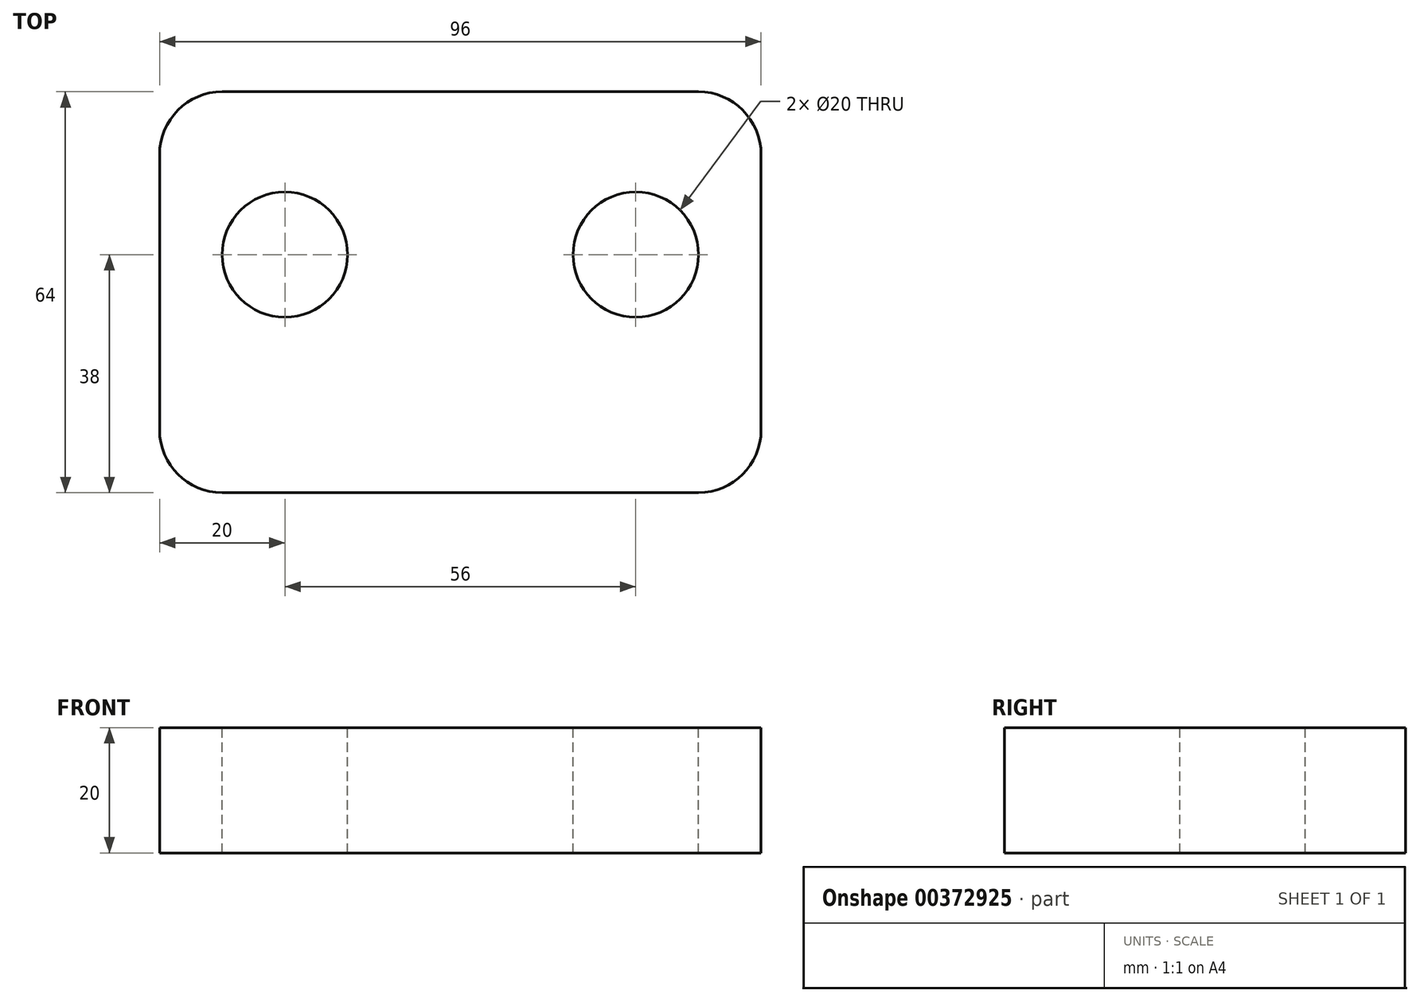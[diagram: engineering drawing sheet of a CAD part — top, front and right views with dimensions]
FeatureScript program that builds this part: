
annotation { "Feature Type Name" : "Feature", "Feature Type Description" : "" }
export const myFeature = defineFeature(function(context is Context, id is Id, definition is map)
    precondition{}
    {
        {
            var Q0;
            Q0=qCreatedBy(makeId("Top.planeOp"),FACE);
            var sketch = newSketch(context, id + "F0", { "sketchPlane" : qUnion([Q0])});
            skLineSegment(sketch, "E0.bottom", {"start": v(48, 32) * mm, "end": v(-48, 32) * mm});
            skLineSegment(sketch, "E0.top", {"start": v(48, -32) * mm, "end": v(-48, -32) * mm});
            skLineSegment(sketch, "E0.left", {"start": v(48, 32) * mm, "end": v(48, -32) * mm});
            skLineSegment(sketch, "E0.right", {"start": v(-48, 32) * mm, "end": v(-48, -32) * mm});
            skPoint(sketch, "E0.middle", {"position": v(0, 0) * mm});
            skSolve(sketch);
        }
        {
            var Q0;
            Q0 = qSketchRegion(id + "F0", true);
            extrude(context, id + "F1", {"entities" : qUnion([Q0]), "depth" : 20 * mm});
        }
        {
            var Q0;
            Q0=makeQuery(id+"F1.opExtrude","SWEPT_EDGE",EDGE,{"disambiguationData":[OSD([sQuery(id+"F0.wireOp",EDGE,"E0.top"),sQuery(id+"F0.wireOp",EDGE,"E0.left")])]});
            var Q1;
            Q1=makeQuery(id+"F1.opExtrude","SWEPT_EDGE",EDGE,{"disambiguationData":[OSD([sQuery(id+"F0.wireOp",EDGE,"E0.bottom"),sQuery(id+"F0.wireOp",EDGE,"E0.left")])]});
            var Q2;
            Q2=makeQuery(id+"F1.opExtrude","SWEPT_EDGE",EDGE,{"disambiguationData":[OSD([sQuery(id+"F0.wireOp",EDGE,"E0.bottom"),sQuery(id+"F0.wireOp",EDGE,"E0.right")])]});
            var Q3;
            Q3=makeQuery(id+"F1.opExtrude","SWEPT_EDGE",EDGE,{"disambiguationData":[OSD([sQuery(id+"F0.wireOp",EDGE,"E0.top"),sQuery(id+"F0.wireOp",EDGE,"E0.right")])]});
            fillet(context, id + "F2", {"entities" : qUnion([Q0, Q1, Q2, Q3]), "radius" : 10 * mm, "tangentPropagation" : true, "allowEdgeOverflow" : false});
        }
        {
            var Q0;
            Q0=makeQuery(id+"F1.opExtrude","CAP_FACE",FACE,{"disambiguationData":[OSD([sQuery(id+"F0.wireOp",EDGE,"E0.bottom"),sQuery(id+"F0.wireOp",EDGE,"E0.top"),sQuery(id+"F0.wireOp",EDGE,"E0.left"),sQuery(id+"F0.wireOp",EDGE,"E0.right")])],"isStart":false});
            var sketch = newSketch(context, id + "F3", { "sketchPlane" : qUnion([Q0])});
            skCircle(sketch, "E1", {"center": v(28, 6) * mm, "radius": 10 * mm});
            skCircle(sketch, "E2", {"center": v(-28, 6) * mm, "radius": 10 * mm});
            skSolve(sketch);
        }
        {
            var Q0;
            Q0=makeQuery(id+"F3.imprint","IMPRINT",FACE,{"disambiguationData":[TD([[makeQuery(id+"F3.imprint","IMPRINT",EDGE,{"derivedFrom":sQuery(id+"F3.wireOp",EDGE,"E1")}),1.0]])]});
            extrude(context, id + "F4", {"entities" : qUnion([Q0]), "operationType" : NewBodyOperationType.REMOVE, "oppositeDirection" : true, "depth" : 25 * mm});
        }
        {
            var Q0;
            Q0=makeQuery(id+"F3.imprint","IMPRINT",FACE,{"disambiguationData":[TD([[makeQuery(id+"F3.imprint","IMPRINT",EDGE,{"derivedFrom":sQuery(id+"F3.wireOp",EDGE,"E2")}),1.0]])]});
            extrude(context, id + "F5", {"entities" : qUnion([Q0]), "operationType" : NewBodyOperationType.REMOVE, "oppositeDirection" : true, "depth" : 55.9 * mm});
        }
    });
